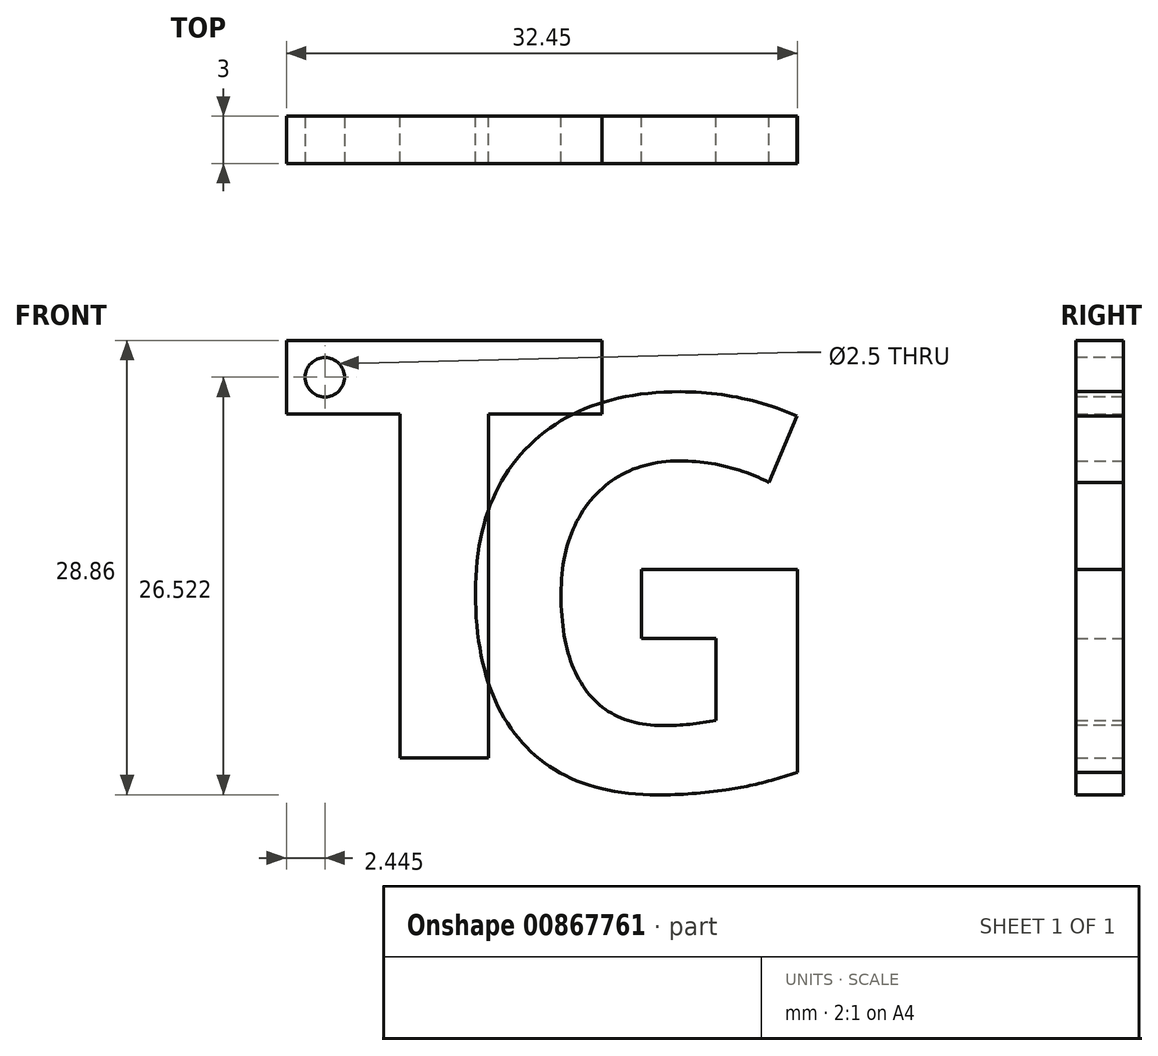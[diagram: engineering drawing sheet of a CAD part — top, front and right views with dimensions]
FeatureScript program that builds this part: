
annotation { "Feature Type Name" : "Feature", "Feature Type Description" : "" }
export const myFeature = defineFeature(function(context is Context, id is Id, definition is map)
    precondition{}
    {
        {
            var Q0;
            Q0=qCreatedBy(makeId("Front.planeOp"),FACE);
            var sketch = newSketch(context, id + "F0", { "sketchPlane" : qUnion([Q0])});
            skText(sketch, "E0", { "text": "T", "fontName": "OpenSans-Bold.ttf"});
            const initialGuessF0  = {"E0": [-0.03354, 0, 1, 0, 0.02675]};
            skSetInitialGuess(sketch, initialGuessF0);
            skSolve(sketch);
        }
        {
            var Q0;
            Q0 = qSketchRegion(id + "F0", true);
            extrude(context, id + "F1", {"entities" : qUnion([Q0]), "depth" : 3 * mm, "offsetDistance" : 25 * mm});
        }
        {
            var Q0;
            Q0=qCreatedBy(makeId("Front.planeOp"),FACE);
            var sketch = newSketch(context, id + "F2", { "sketchPlane" : qUnion([Q0])});
            skText(sketch, "E1", { "text": "G\n", "fontName": "OpenSans-Bold.ttf"});
            const initialGuessF2  = {"E1": [-0.06232, 0, 1, 0, 0.02512]};
            skSetInitialGuess(sketch, initialGuessF2);
            skSolve(sketch);
        }
        {
            var Q0;
            Q0 = qSketchRegion(id + "F2", true);
            extrude(context, id + "F3", {"entities" : qUnion([Q0]), "depth" : 3 * mm, "offsetDistance" : 25 * mm});
        }
        {
            var Q0;
            Q0=makeQuery(id+"F3.opExtrude","SWEPT_BODY",BODY,{"disambiguationData":[OSD([sQuery(id+"F2.wireOp",EDGE,"E1.sketch_text.stroke-0"),sQuery(id+"F2.wireOp",EDGE,"E1.sketch_text.stroke-1"),sQuery(id+"F2.wireOp",EDGE,"E1.sketch_text.stroke-2"),sQuery(id+"F2.wireOp",EDGE,"E1.sketch_text.stroke-3"),sQuery(id+"F2.wireOp",EDGE,"E1.sketch_text.stroke-4"),sQuery(id+"F2.wireOp",EDGE,"E1.sketch_text.stroke-5"),sQuery(id+"F2.wireOp",EDGE,"E1.sketch_text.stroke-6"),sQuery(id+"F2.wireOp",EDGE,"E1.sketch_text.stroke-7"),sQuery(id+"F2.wireOp",EDGE,"E1.sketch_text.stroke-8"),sQuery(id+"F2.wireOp",EDGE,"E1.sketch_text.stroke-9"),sQuery(id+"F2.wireOp",EDGE,"E1.sketch_text.stroke-10"),sQuery(id+"F2.wireOp",EDGE,"E1.sketch_text.stroke-11"),sQuery(id+"F2.wireOp",EDGE,"E1.sketch_text.stroke-12"),sQuery(id+"F2.wireOp",EDGE,"E1.sketch_text.stroke-13"),sQuery(id+"F2.wireOp",EDGE,"E1.sketch_text.stroke-14"),sQuery(id+"F2.wireOp",EDGE,"E1.sketch_text.stroke-15"),sQuery(id+"F2.wireOp",EDGE,"E1.sketch_text.stroke-16"),sQuery(id+"F2.wireOp",EDGE,"E1.sketch_text.stroke-17"),sQuery(id+"F2.wireOp",EDGE,"E1.sketch_text.stroke-18")])]});
            transform(context, id + "F4", {"entities" : qUnion([Q0]), "transformType" : TransformType.TRANSLATION_3D, "dx" : 39.5 * mm, "dy" : 0 * mm, "dz" : -2 * mm, "makeCopy" : false});
        }
        {
            var Q0;
            Q0=makeQuery(id+"F1.opExtrude","CAP_FACE",FACE,{"disambiguationData":[OSD([sQuery(id+"F0.wireOp",EDGE,"E0.sketch_text.stroke-0"),sQuery(id+"F0.wireOp",EDGE,"E0.sketch_text.stroke-1"),sQuery(id+"F0.wireOp",EDGE,"E0.sketch_text.stroke-2"),sQuery(id+"F0.wireOp",EDGE,"E0.sketch_text.stroke-3"),sQuery(id+"F0.wireOp",EDGE,"E0.sketch_text.stroke-4"),sQuery(id+"F0.wireOp",EDGE,"E0.sketch_text.stroke-5"),sQuery(id+"F0.wireOp",EDGE,"E0.sketch_text.stroke-6"),sQuery(id+"F0.wireOp",EDGE,"E0.sketch_text.stroke-7")])],"isStart":false});
            var sketch = newSketch(context, id + "F5", { "sketchPlane" : qUnion([Q0])});
            skLineSegment(sketch, "E2", {"start": v(-32.8, 26.52) * mm, "end": v(-32.8, 24.18) * mm});
            skLineSegment(sketch, "E3", {"start": v(-32.8, 24.18) * mm, "end": v(-30.36, 24.18) * mm});
            skCircle(sketch, "E4", {"center": v(-30.36, 24.18) * mm, "radius": 1.25 * mm});
            skSolve(sketch);
        }
        {
            var Q0;
            Q0 = qSketchRegion(id + "F5", true);
            extrude(context, id + "F6", {"entities" : qUnion([Q0]), "operationType" : NewBodyOperationType.REMOVE, "oppositeDirection" : true, "depth" : 25 * mm, "offsetDistance" : 25 * mm});
        }
    });
